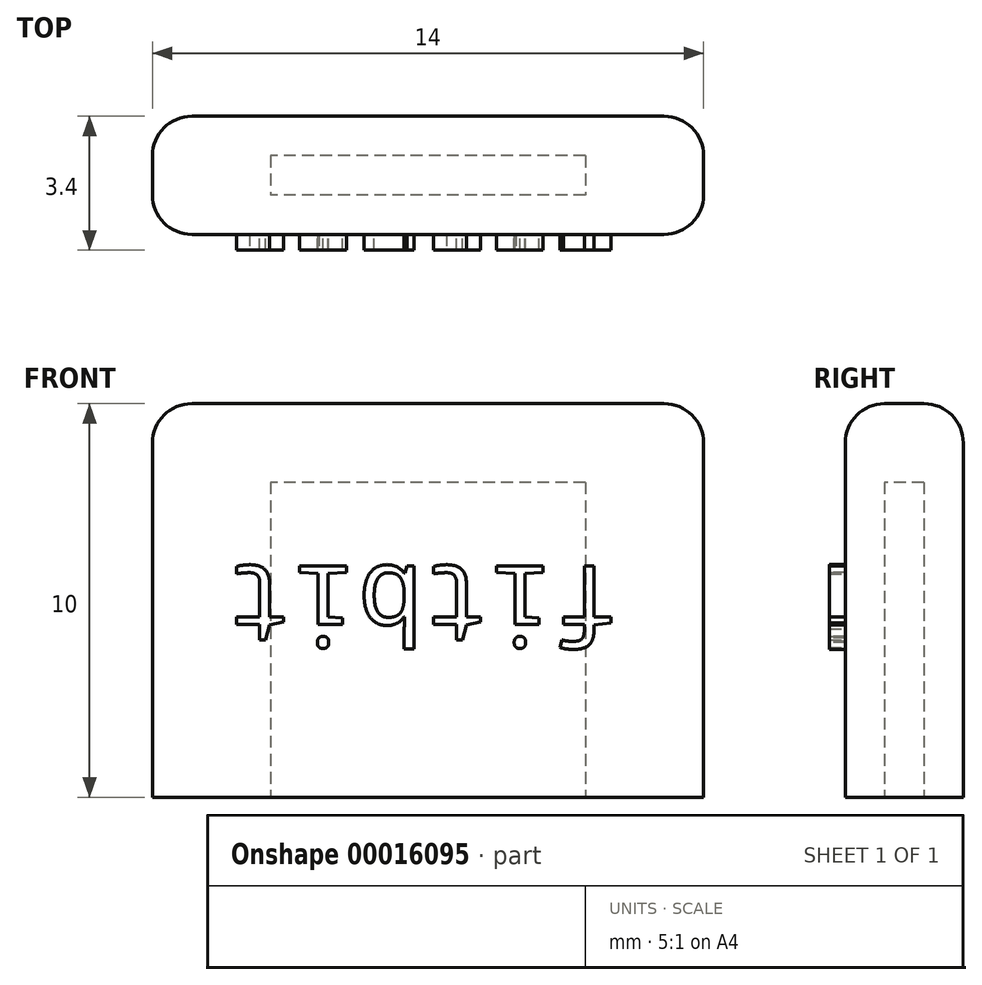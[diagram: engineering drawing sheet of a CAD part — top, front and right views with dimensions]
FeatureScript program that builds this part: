
annotation { "Feature Type Name" : "Feature", "Feature Type Description" : "" }
export const myFeature = defineFeature(function(context is Context, id is Id, definition is map)
    precondition{}
    {
        {
            var Q0;
            Q0=qCreatedBy(makeId("Top.planeOp"),FACE);
            var sketch = newSketch(context, id + "F0", { "sketchPlane" : qUnion([Q0])});
            skLineSegment(sketch, "E0.rect.bottom", {"start": v(7, 1.5) * mm, "end": v(-7, 1.5) * mm});
            skLineSegment(sketch, "E0.rect.top", {"start": v(7, -1.5) * mm, "end": v(-7, -1.5) * mm});
            skLineSegment(sketch, "E0.rect.left", {"start": v(7, 1.5) * mm, "end": v(7, -1.5) * mm});
            skLineSegment(sketch, "E0.rect.right", {"start": v(-7, 1.5) * mm, "end": v(-7, -1.5) * mm});
            skPoint(sketch, "E0.rect.middle", {"position": v(0, 0) * mm});
            skLineSegment(sketch, "E1.rect.bottom", {"start": v(4, 0.5) * mm, "end": v(-4, 0.5) * mm});
            skLineSegment(sketch, "E1.rect.top", {"start": v(4, -0.5) * mm, "end": v(-4, -0.5) * mm});
            skLineSegment(sketch, "E1.rect.left", {"start": v(4, 0.5) * mm, "end": v(4, -0.5) * mm});
            skLineSegment(sketch, "E1.rect.right", {"start": v(-4, 0.5) * mm, "end": v(-4, -0.5) * mm});
            skSolve(sketch);
        }
        {
            var Q0;
            Q0 = qSketchRegion(id + "F0", true);
            var Q1;
            Q1=makeQuery(id+"F0.imprint","IMPRINT",FACE,{"disambiguationData":[TD([[makeQuery(id+"F0.imprint","IMPRINT",EDGE,{"derivedFrom":sQuery(id+"F0.wireOp",EDGE,"E1.rect.bottom")}),1.0]])]});
            extrude(context, id + "F1", {"entities" : qUnion([Q0, Q1]), "depth" : 10 * mm});
        }
        {
            var Q0;
            Q0=makeQuery(id+"F0.imprint","IMPRINT",FACE,{"disambiguationData":[TD([[makeQuery(id+"F0.imprint","IMPRINT",EDGE,{"derivedFrom":sQuery(id+"F0.wireOp",EDGE,"E1.rect.bottom")}),1.0]])]});
            extrude(context, id + "F2", {"entities" : qUnion([Q0]), "operationType" : NewBodyOperationType.REMOVE, "depth" : 8 * mm});
        }
        {
            var Q0;
            Q0=makeQuery(id+"F1.opExtrude","CAP_EDGE",EDGE,{"disambiguationData":[OSD([sQuery(id+"F0.wireOp",EDGE,"E0.rect.right")])],"isStart":false});
            var Q1;
            Q1=makeQuery(id+"F1.opExtrude","CAP_EDGE",EDGE,{"disambiguationData":[OSD([sQuery(id+"F0.wireOp",EDGE,"E0.rect.left")])],"isStart":false});
            var Q2;
            Q2=makeQuery(id+"F1.opExtrude","CAP_EDGE",EDGE,{"disambiguationData":[OSD([sQuery(id+"F0.wireOp",EDGE,"E0.rect.top")])],"isStart":false});
            var Q3;
            Q3=makeQuery(id+"F1.opExtrude","CAP_EDGE",EDGE,{"disambiguationData":[OSD([sQuery(id+"F0.wireOp",EDGE,"E0.rect.bottom")])],"isStart":false});
            var Q4;
            Q4=makeQuery(id+"F1.opExtrude","SWEPT_EDGE",EDGE,{"disambiguationData":[OSD([sQuery(id+"F0.wireOp",EDGE,"E0.rect.top"),sQuery(id+"F0.wireOp",EDGE,"E0.rect.right")])]});
            var Q5;
            Q5=makeQuery(id+"F1.opExtrude","SWEPT_EDGE",EDGE,{"disambiguationData":[OSD([sQuery(id+"F0.wireOp",EDGE,"E0.rect.bottom"),sQuery(id+"F0.wireOp",EDGE,"E0.rect.right")])]});
            var Q6;
            Q6=makeQuery(id+"F1.opExtrude","SWEPT_EDGE",EDGE,{"disambiguationData":[OSD([sQuery(id+"F0.wireOp",EDGE,"E0.rect.top"),sQuery(id+"F0.wireOp",EDGE,"E0.rect.left")])]});
            var Q7;
            Q7=makeQuery(id+"F1.opExtrude","SWEPT_EDGE",EDGE,{"disambiguationData":[OSD([sQuery(id+"F0.wireOp",EDGE,"E0.rect.bottom"),sQuery(id+"F0.wireOp",EDGE,"E0.rect.left")])]});
            fillet(context, id + "F3", {"entities" : qUnion([Q0, Q1, Q2, Q3, Q4, Q5, Q6, Q7]), "radius" : 1 * mm, "tangentPropagation" : true, "allowEdgeOverflow" : false});
        }
        {
            var Q0;
            Q0=makeQuery(id+"F1.opExtrude","SWEPT_FACE",FACE,{"disambiguationData":[OSD([sQuery(id+"F0.wireOp",EDGE,"E0.rect.top")])]});
            var sketch = newSketch(context, id + "F4", { "sketchPlane" : qUnion([Q0])});
            skText(sketch, "E2", { "text": "fitbit", "fontName": "DroidSansMono.ttf"});
            skLineSegment(sketch, "E3.0", {"start": v(-6, 9) * mm, "end": v(-6, 0) * mm});
            skLineSegment(sketch, "E4", {"start": v(-4.86, 5.88) * mm, "end": v(-6, 5.88) * mm, "construction": true});
            skLineSegment(sketch, "E5", {"start": v(4.86, 5.88) * mm, "end": v(6, 5.88) * mm, "construction": true});
            const initialGuessF4  = {"E2": [0.00486, 0.00588, -1, 0, 0.002]};
            skSetInitialGuess(sketch, initialGuessF4);
            skSolve(sketch);
        }
        {
            var Q0;
            Q0 = qSketchRegion(id + "F4", true);
            extrude(context, id + "F5", {"entities" : qUnion([Q0]), "operationType" : NewBodyOperationType.ADD, "depth" : .4 * mm});
        }
    });
